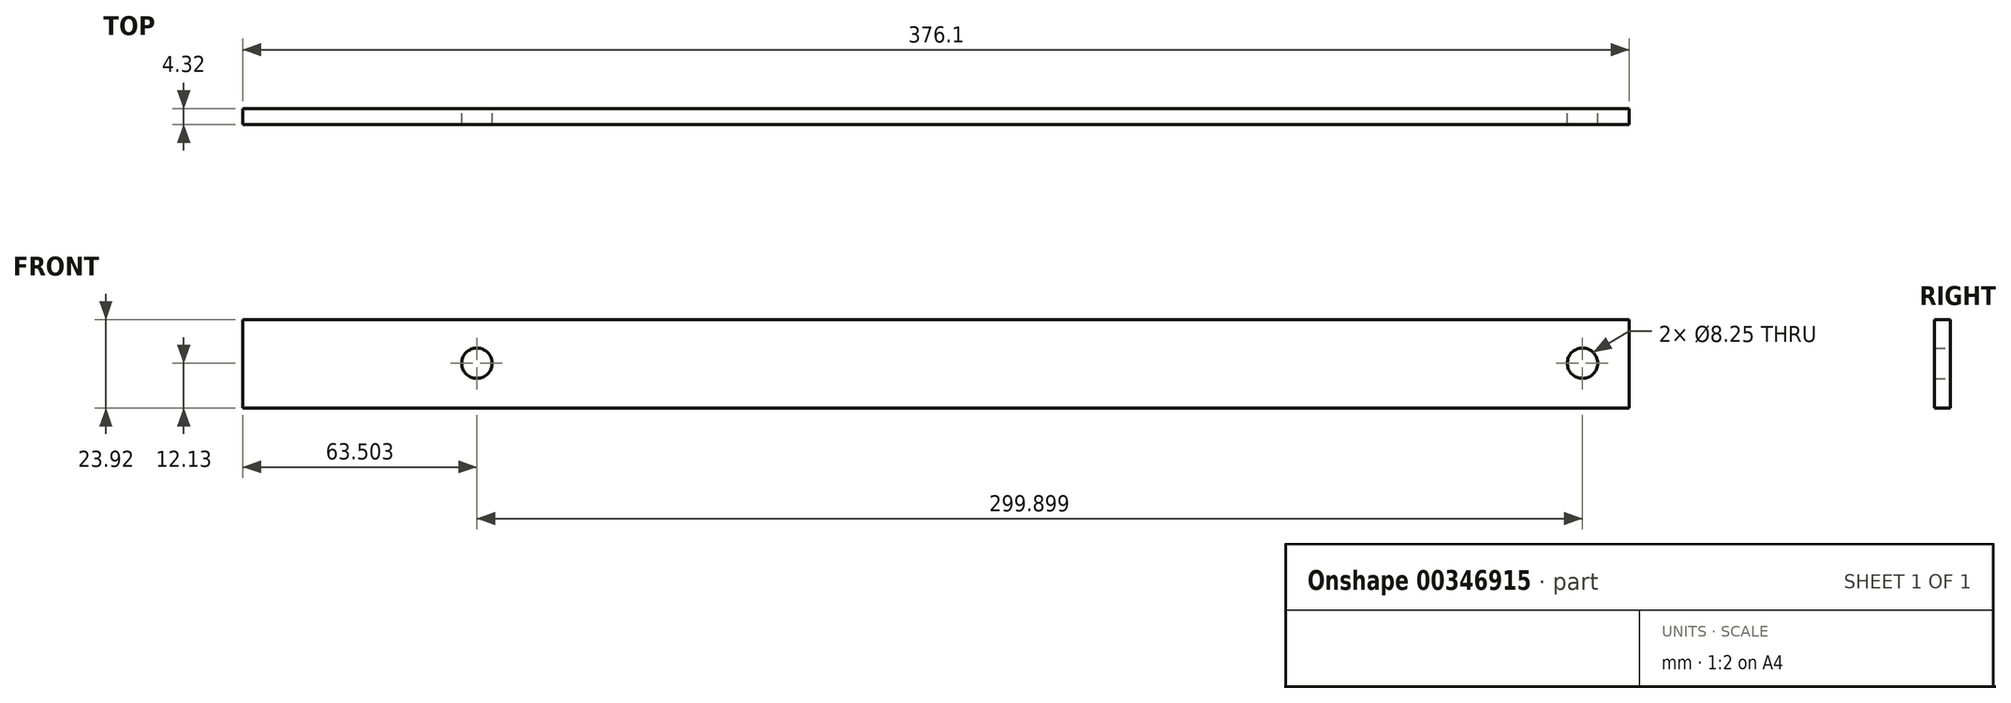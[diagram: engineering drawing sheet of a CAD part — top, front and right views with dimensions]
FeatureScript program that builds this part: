
annotation { "Feature Type Name" : "Feature", "Feature Type Description" : "" }
export const myFeature = defineFeature(function(context is Context, id is Id, definition is map)
    precondition{}
    {
        {
            var Q0;
            Q0=qCreatedBy(makeId("Front.planeOp"),FACE);
            var sketch = newSketch(context, id + "F0", { "sketchPlane" : qUnion([Q0])});
            skCircle(sketch, "E0", {"center": v(92.31, 0) * mm, "radius": 4.12 * mm});
            skCircle(sketch, "E1", {"center": v(-207.59, 0) * mm, "radius": 4.12 * mm});
            skLineSegment(sketch, "E2.bottom", {"start": v(-271.09, 11.8) * mm, "end": v(105.01, 11.8) * mm});
            skLineSegment(sketch, "E2.top", {"start": v(-271.09, -12.13) * mm, "end": v(105.01, -12.13) * mm});
            skLineSegment(sketch, "E2.left", {"start": v(-271.09, 11.8) * mm, "end": v(-271.09, -12.13) * mm});
            skLineSegment(sketch, "E2.right", {"start": v(105.01, 11.8) * mm, "end": v(105.01, -12.13) * mm});
            skSolve(sketch);
        }
        {
            var Q0;
            Q0 = qSketchRegion(id + "F0", true);
            extrude(context, id + "F1", {"entities" : qUnion([Q0]), "depth" : 4.32 * mm});
        }
    });
